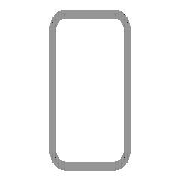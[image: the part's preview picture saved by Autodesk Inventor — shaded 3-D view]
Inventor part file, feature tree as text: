
AUTODESK INVENTOR PART (.ipt)
format: ipt  version: 2025 (Build 290162010, 162A)  size: 136,192 bytes
history: native  units: mm (DEFAULTED — no unit token found)
features: other x4, sketch x1, plane x1
ambient origin geometry x8: Origin, YZ Plane, XZ Plane, XY Plane, X Axis, Y Axis, Z Axis, Center Point
bodies: Solid1 (feature_tree), Body (feature_tree)
feature tree (6):
  parser-record x1  (decoder bookkeeping rows leaked as tree rows — omitted from the tree; the rows remain in map.json)
  other  "Driven Length"
  other  "Start Plane"
  other  "End Plane"
  sketch  "Sketch3"  dims[d3=1420.0mm d4=0.0mm d7=6.0mm d9=40.0mm d11=60.0mm d12=3.0mm d13=40.0mm d14=1460.0mm d15=20.0mm d16=30.0mm d17=90.0deg d18=1420.0mm]
  plane  "Work Plane3"
